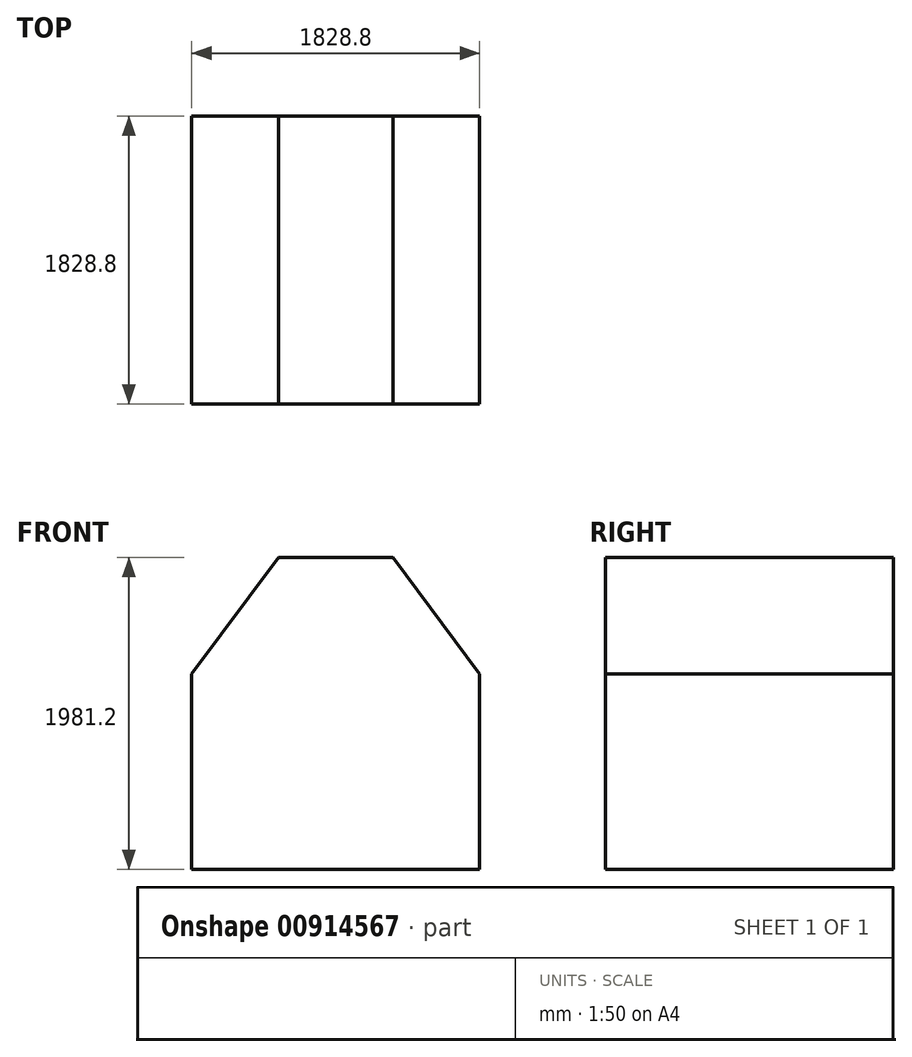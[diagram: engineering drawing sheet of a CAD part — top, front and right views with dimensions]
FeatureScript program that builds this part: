
annotation { "Feature Type Name" : "Feature", "Feature Type Description" : "" }
export const myFeature = defineFeature(function(context is Context, id is Id, definition is map)
    precondition{}
    {
        {
            var Q0;
            Q0=qCreatedBy(makeId("Front.planeOp"),FACE);
            var sketch = newSketch(context, id + "F0", { "sketchPlane" : qUnion([Q0])});
            skLineSegment(sketch, "E0", {"start": v(0, 0) * mm, "end": v(1828.8, 0) * mm});
            skLineSegment(sketch, "E1", {"start": v(914.4, 0) * mm, "end": v(914.4, 1981.2) * mm, "construction": true});
            skLineSegment(sketch, "E2", {"start": v(0, 0) * mm, "end": v(0, 245.47) * mm});
            skLineSegment(sketch, "E3", {"start": v(0, 245.47) * mm, "end": v(0, 1243.05) * mm});
            skLineSegment(sketch, "E4", {"start": v(1828.8, 0) * mm, "end": v(1828.8, 245.47) * mm});
            skLineSegment(sketch, "E5", {"start": v(1828.8, 245.47) * mm, "end": v(1828.8, 1243.05) * mm});
            skLineSegment(sketch, "E6", {"start": v(549.31, 1981.2) * mm, "end": v(1279.47, 1981.2) * mm});
            skLineSegment(sketch, "E7", {"start": v(549.31, 1981.2) * mm, "end": v(0, 1243.05) * mm});
            skLineSegment(sketch, "E8", {"start": v(1279.47, 1981.2) * mm, "end": v(1828.8, 1243.05) * mm});
            skPoint(sketch, "E9", {"position": v(549.31, 1981.2) * mm});
            skPoint(sketch, "E10", {"position": v(1279.47, 1981.2) * mm});
            skLineSegment(sketch, "E11.top", {"start": v(0, 0) * mm, "end": v(304.8, 0) * mm});
            skLineSegment(sketch, "E11.left", {"start": v(0, 245.47) * mm, "end": v(0, 0) * mm});
            skLineSegment(sketch, "E12.top", {"start": v(1828.8, 0) * mm, "end": v(1524, 0) * mm});
            skLineSegment(sketch, "E12.left", {"start": v(1828.8, 245.47) * mm, "end": v(1828.8, 0) * mm});
            skPoint(sketch, "E13", {"position": v(304.8, 938.25) * mm});
            skLineSegment(sketch, "E14", {"start": v(0, 245.47) * mm, "end": v(0, 914.4) * mm, "construction": true});
            skLineSegment(sketch, "E15", {"start": v(0, 914.4) * mm, "end": v(0, 1243.05) * mm, "construction": true});
            skLineSegment(sketch, "E16", {"start": v(0, 1243.05) * mm, "end": v(549.31, 1981.2) * mm, "construction": true});
            skLineSegment(sketch, "E17", {"start": v(0, 1243.05) * mm, "end": v(0, 1243.05) * mm});
            skLineSegment(sketch, "E18.bottom", {"start": v(2679.28, 1828.8) * mm, "end": v(4508.08, 1828.8) * mm, "construction": true});
            skLineSegment(sketch, "E18.top", {"start": v(2679.28, 0) * mm, "end": v(4508.08, 0) * mm, "construction": true});
            skLineSegment(sketch, "E18.left", {"start": v(2679.28, 1828.8) * mm, "end": v(2679.28, 0) * mm, "construction": true});
            skLineSegment(sketch, "E18.right", {"start": v(4508.08, 1828.8) * mm, "end": v(4508.08, 0) * mm, "construction": true});
            skLineSegment(sketch, "E19.bottom", {"start": v(2679.28, 1828.8) * mm, "end": v(2984.08, 1828.8) * mm, "construction": true});
            skLineSegment(sketch, "E19.left", {"start": v(2679.28, 1828.8) * mm, "end": v(2679.28, 1219.2) * mm, "construction": true});
            skLineSegment(sketch, "E19.right", {"start": v(2984.08, 1828.8) * mm, "end": v(2984.08, 1219.2) * mm, "construction": true});
            skLineSegment(sketch, "E20.bottom", {"start": v(2679.28, 0) * mm, "end": v(2984.08, 0) * mm, "construction": true});
            skLineSegment(sketch, "E20.left", {"start": v(2679.28, 0) * mm, "end": v(2679.28, 609.6) * mm, "construction": true});
            skLineSegment(sketch, "E20.right", {"start": v(2984.08, 0) * mm, "end": v(2984.08, 609.6) * mm, "construction": true});
            skLineSegment(sketch, "E21", {"start": v(2984.08, 1219.2) * mm, "end": v(2984.08, 609.6) * mm, "construction": true});
            skLineSegment(sketch, "E22", {"start": v(4203.28, 1828.8) * mm, "end": v(4203.28, 0) * mm, "construction": true});
            skLineSegment(sketch, "E23.bottom", {"start": v(3256.68, 598.46) * mm, "end": v(3958.36, 598.46) * mm, "construction": true});
            skLineSegment(sketch, "E23.top", {"start": v(3256.68, 240.34) * mm, "end": v(3958.36, 240.34) * mm, "construction": true});
            skLineSegment(sketch, "E23.left", {"start": v(3256.68, 598.46) * mm, "end": v(3256.68, 240.34) * mm, "construction": true});
            skLineSegment(sketch, "E23.right", {"start": v(3958.36, 598.46) * mm, "end": v(3958.36, 240.34) * mm, "construction": true});
            skPoint(sketch, "E24", {"position": v(1828.8, 1243.05) * mm});
            skSolve(sketch);
        }
        {
            var Q0;
            Q0=makeQuery(id+"F0.imprint","IMPRINT",FACE,{"disambiguationData":[TD([[makeQuery(id+"F0.imprint","IMPRINT",EDGE,{"derivedFrom":sQuery(id+"F0.wireOp",EDGE,"E0")}),1.0]])]});
            extrude(context, id + "F1", {"entities" : qUnion([Q0]), "depth" : 1828.8 * mm, "offsetDistance" : 25.4 * mm});
        }
    });
